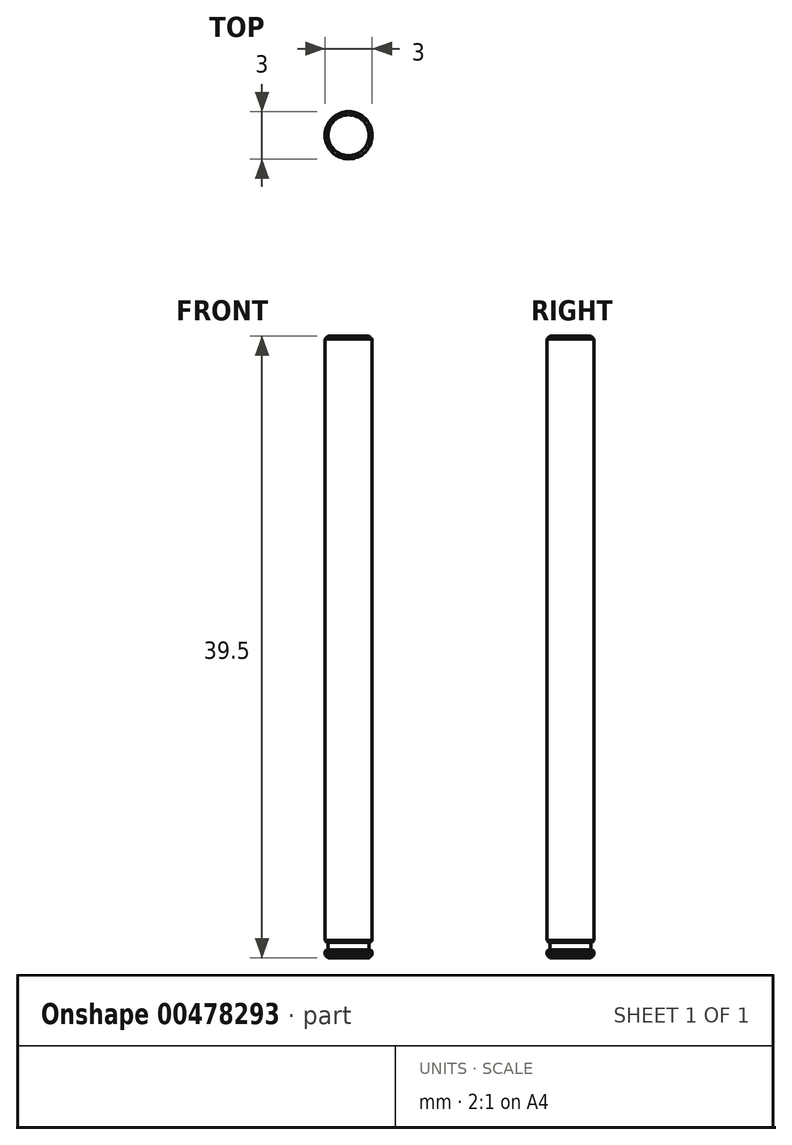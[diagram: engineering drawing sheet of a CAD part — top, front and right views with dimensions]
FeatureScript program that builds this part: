
annotation { "Feature Type Name" : "Feature", "Feature Type Description" : "" }
export const myFeature = defineFeature(function(context is Context, id is Id, definition is map)
    precondition{}
    {
        {
            var Q0;
            Q0=qCreatedBy(makeId("Top.planeOp"),FACE);
            var sketch = newSketch(context, id + "F0", { "sketchPlane" : qUnion([Q0])});
            skCircle(sketch, "E0", {"center": v(0, 0) * mm, "radius": 1.5 * mm});
            skCircle(sketch, "E1.0", {"center": v(0, 0) * mm, "radius": 1.3 * mm});
            skSolve(sketch);
        }
        {
            var Q0;
            Q0=qSketchRegion(id+"F0",true);
            var Q1;
            Q1=makeQuery(id+"F0.imprint","IMPRINT",FACE,{"disambiguationData":[TD([[makeQuery(id+"F0.imprint","IMPRINT",EDGE,{"derivedFrom":sQuery(id+"F0.wireOp",EDGE,"E1.0")}),1.0]])]});
            extrude(context, id + "F1", {"entities" : qUnion([Q0, Q1]), "depth" : 38.5 * mm});
        }
        {
            var Q0;
            Q0=makeQuery(id+"F0.imprint","IMPRINT",FACE,{"disambiguationData":[TD([[makeQuery(id+"F0.imprint","IMPRINT",EDGE,{"derivedFrom":sQuery(id+"F0.wireOp",EDGE,"E1.0")}),1.0]])]});
            extrude(context, id + "F2", {"entities" : qUnion([Q0]), "operationType" : NewBodyOperationType.ADD, "oppositeDirection" : true, "depth" : 1 * mm});
        }
        {
            var Q0;
            Q0=qSketchRegion(id+"F0",true);
            extrude(context, id + "F3", {"entities" : qUnion([Q0]), "operationType" : NewBodyOperationType.ADD, "oppositeDirection" : true, "depth" : 1 * mm, "hasSecondDirection" : true, "secondDirectionOppositeDirection" : true, "secondDirectionDepth" : 0.5 * mm});
        }
        {
            var Q0;
            Q0=makeQuery(id+"F3.opExtrude","CAP_EDGE",EDGE,{"disambiguationData":[OSD([sQuery(id+"F0.wireOp",EDGE,"E0")])],"isStart":false});
            var Q1;
            Q1=makeQuery(id+"F1.opExtrude","CAP_EDGE",EDGE,{"disambiguationData":[OSD([sQuery(id+"F0.wireOp",EDGE,"E0")])],"isStart":false});
            chamfer(context, id + "F4", {"entities" : qUnion([Q0, Q1]), "width" : 0.2 * mm, "tangentPropagation" : true});
        }
        {
            var Q0;
            Q0=makeQuery(id+"F3.opExtrude","CAP_EDGE",EDGE,{"disambiguationData":[OSD([sQuery(id+"F0.wireOp",EDGE,"E0")])],"isStart":true});
            var Q1;
            Q1=makeQuery(id+"F1.opExtrude","CAP_EDGE",EDGE,{"disambiguationData":[OSD([sQuery(id+"F0.wireOp",EDGE,"E0")])],"isStart":true});
            chamfer(context, id + "F5", {"entities" : qUnion([Q0, Q1]), "width" : 0.1 * mm, "tangentPropagation" : true});
        }
    });
